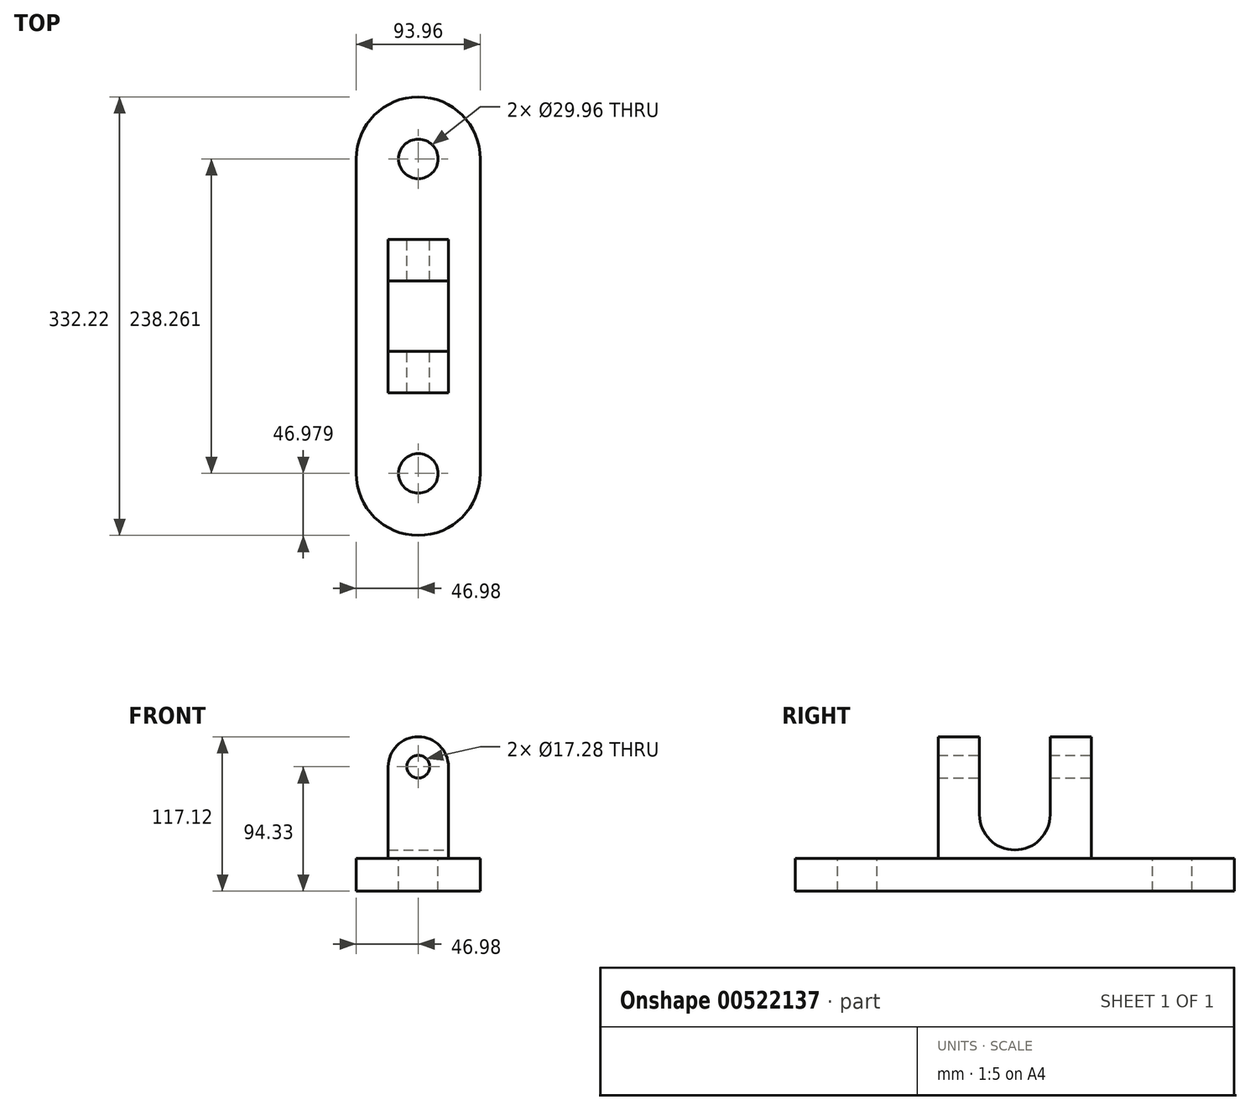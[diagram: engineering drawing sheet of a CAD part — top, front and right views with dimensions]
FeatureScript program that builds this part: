
annotation { "Feature Type Name" : "Feature", "Feature Type Description" : "" }
export const myFeature = defineFeature(function(context is Context, id is Id, definition is map)
    precondition{}
    {
        {
            var Q0;
            Q0=qCreatedBy(makeId("Top.planeOp"),FACE);
            var sketch = newSketch(context, id + "F0", { "sketchPlane" : qUnion([Q0])});
            skLineSegment(sketch, "E0.left", {"start": v(46.98, -119.13) * mm, "end": v(46.98, 119.13) * mm});
            skLineSegment(sketch, "E0.right", {"start": v(-46.98, -119.13) * mm, "end": v(-46.98, 119.13) * mm});
            skPoint(sketch, "E0.middle", {"position": v(0, 0) * mm});
            skArc(sketch, "E1", {"start": v(46.98, 119.13) * mm, "mid": v(0, 166.1) * mm, "end": v(-46.98, 119.13) * mm});
            skArc(sketch, "E2", {"start": v(-46.98, -119.13) * mm, "mid": v(0, -166.1) * mm, "end": v(46.98, -119.13) * mm});
            skCircle(sketch, "E3", {"center": v(0, 119.13) * mm, "radius": 14.98 * mm});
            skCircle(sketch, "E4.MirrorC", {"center": v(0, -119.13) * mm, "radius": 14.98 * mm});
            skSolve(sketch);
        }
        {
            var Q0;
            Q0=makeQuery(id+"F0.imprint","IMPRINT",FACE,{"disambiguationData":[TD([[makeQuery(id+"F0.imprint","IMPRINT",EDGE,{"derivedFrom":sQuery(id+"F0.wireOp",EDGE,"E0.left")}),1.0]])]});
            extrude(context, id + "F1", {"entities" : qUnion([Q0]), "oppositeDirection" : true, "depth" : 25 * mm, "offsetDistance" : 25 * mm});
        }
        {
            var Q0;
            Q0=qCreatedBy(makeId("Front.planeOp"),FACE);
            var sketch = newSketch(context, id + "F2", { "sketchPlane" : qUnion([Q0])});
            skLineSegment(sketch, "E5.bottom", {"start": v(-22.8, 0) * mm, "end": v(22.8, 0) * mm});
            skLineSegment(sketch, "E5.left", {"start": v(-22.8, 0) * mm, "end": v(-22.8, 69.33) * mm});
            skLineSegment(sketch, "E5.right", {"start": v(22.8, 0) * mm, "end": v(22.8, 69.33) * mm});
            skLineSegment(sketch, "E6.0.0", {"start": v(46.98, 0) * mm, "end": v(-46.98, 0) * mm, "construction": true});
            skLineSegment(sketch, "E6.0.1", {"start": v(-46.98, 0) * mm, "end": v(-46.98, -25) * mm, "construction": true});
            skLineSegment(sketch, "E6.0.2", {"start": v(-46.98, -25) * mm, "end": v(46.98, -25) * mm, "construction": true});
            skLineSegment(sketch, "E6.0.3", {"start": v(46.98, -25) * mm, "end": v(46.98, 0) * mm, "construction": true});
            skArc(sketch, "E7", {"start": v(22.8, 69.33) * mm, "mid": v(0, 92.12) * mm, "end": v(-22.8, 69.33) * mm});
            skCircle(sketch, "E8", {"center": v(0, 69.33) * mm, "radius": 8.64 * mm});
            skSolve(sketch);
        }
        {
            var Q0;
            Q0=makeQuery(id+"F2.imprint","IMPRINT",FACE,{"disambiguationData":[TD([[makeQuery(id+"F2.imprint","IMPRINT",EDGE,{"derivedFrom":sQuery(id+"F2.wireOp",EDGE,"E5.bottom")}),1.0]])]});
            extrude(context, id + "F3", {"entities" : qUnion([Q0]), "operationType" : NewBodyOperationType.ADD, "endBound" : BoundingType.SYMMETRIC, "depth" : 116 * mm, "offsetDistance" : 25 * mm});
        }
        {
            var Q0;
            Q0=makeQuery(id+"F3.opExtrude","SWEPT_FACE",FACE,{"disambiguationData":[OSD([sQuery(id+"F2.wireOp",EDGE,"E5.right")])]});
            var sketch = newSketch(context, id + "F4", { "sketchPlane" : qUnion([Q0])});
            skLineSegment(sketch, "E9.bottom", {"start": v(-26.7, 69.33) * mm, "end": v(26.7, 69.33) * mm});
            skLineSegment(sketch, "E9.left", {"start": v(-26.7, 69.33) * mm, "end": v(-26.7, 32.96) * mm});
            skLineSegment(sketch, "E9.right", {"start": v(26.7, 69.33) * mm, "end": v(26.7, 32.96) * mm});
            skArc(sketch, "E10", {"start": v(-26.7, 32.96) * mm, "mid": v(0, 6.26) * mm, "end": v(26.7, 32.96) * mm});
            skSolve(sketch);
        }
        {
            var Q0;
            Q0=makeQuery(id+"F4.imprint","IMPRINT",FACE,{"disambiguationData":[TD([[makeQuery(id+"F4.imprint","IMPRINT",EDGE,{"derivedFrom":sQuery(id+"F4.wireOp",EDGE,"E9.bottom")}),-1.0]])]});
            extrude(context, id + "F5", {"entities" : qUnion([Q0]), "operationType" : NewBodyOperationType.REMOVE, "endBound" : BoundingType.THROUGH_ALL, "oppositeDirection" : true, "depth" : 25 * mm, "offsetDistance" : 25 * mm});
        }
        {
            var Q0;
            Q0=makeQuery(id+"F5.boolean.opBoolean","COPY",FACE,{"disambiguationData":[TD([makeQuery(id+"F3.opExtrude","SWEPT_FACE",FACE,{"disambiguationData":[OSD([sQuery(id+"F2.wireOp",EDGE,"E5.right")])]})])],"derivedFrom":makeQuery(id+"F5.opExtrude","SWEPT_FACE",FACE,{"disambiguationData":[OSD([sQuery(id+"F4.wireOp",EDGE,"E9.bottom")])]})});
            var Q1;
            Q1=makeQuery(id+"F5.boolean.opBoolean","COPY",FACE,{"disambiguationData":[TD([makeQuery(id+"F3.opExtrude","SWEPT_FACE",FACE,{"disambiguationData":[OSD([sQuery(id+"F2.wireOp",EDGE,"E5.left")])]})])],"derivedFrom":makeQuery(id+"F5.opExtrude","SWEPT_FACE",FACE,{"disambiguationData":[OSD([sQuery(id+"F4.wireOp",EDGE,"E9.bottom")])]})});
            extrude(context, id + "F6", {"entities" : qUnion([Q0, Q1]), "operationType" : NewBodyOperationType.REMOVE, "oppositeDirection" : true, "depth" : 25 * mm, "offsetDistance" : 25 * mm});
        }
        {
            var Q0;
            {var subQ0=sQuery(id+"F4.wireOp",EDGE,"E9.bottom");var subQ1=sQuery(id+"F2.wireOp",EDGE,"E8");Q0=makeQuery(id+"F6.boolean.opBoolean","COPY",FACE,{"derivedFrom":makeQuery(id+"F6.opExtrude","SWEPT_FACE",FACE,{"disambiguationData":[OSD([subQ1,subQ0]),TDD([makeQuery(id+"F5.boolean.opBoolean","INTERSECT",EDGE,{"disambiguationData":[OD(0.0)],"derivedFrom":[makeQuery(id+"F3.opExtrude","SWEPT_FACE",FACE,{"disambiguationData":[OSD([subQ1])]}),makeQuery(id+"F5.opExtrude","SWEPT_FACE",FACE,{"disambiguationData":[OSD([subQ0])]})]})])]})});}
            extrude(context, id + "F7", {"entities" : qUnion([Q0]), "operationType" : NewBodyOperationType.REMOVE, "endBound" : BoundingType.THROUGH_ALL, "oppositeDirection" : true, "depth" : 25 * mm, "offsetDistance" : 25 * mm});
        }
        {
            var Q0;
            Q0=makeQuery(id+"F7.boolean.opBoolean","COPY",FACE,{"derivedFrom":makeQuery(id+"F7.opExtrude","SWEPT_FACE",FACE,{"disambiguationData":[OSD([sQuery(id+"F2.wireOp",EDGE,"E7"),sQuery(id+"F2.wireOp",EDGE,"E8"),sQuery(id+"F4.wireOp",EDGE,"E9.bottom")])]})});
            extrude(context, id + "F8", {"entities" : qUnion([Q0]), "operationType" : NewBodyOperationType.REMOVE, "oppositeDirection" : true, "depth" : 25 * mm, "offsetDistance" : 25 * mm});
        }
    });
